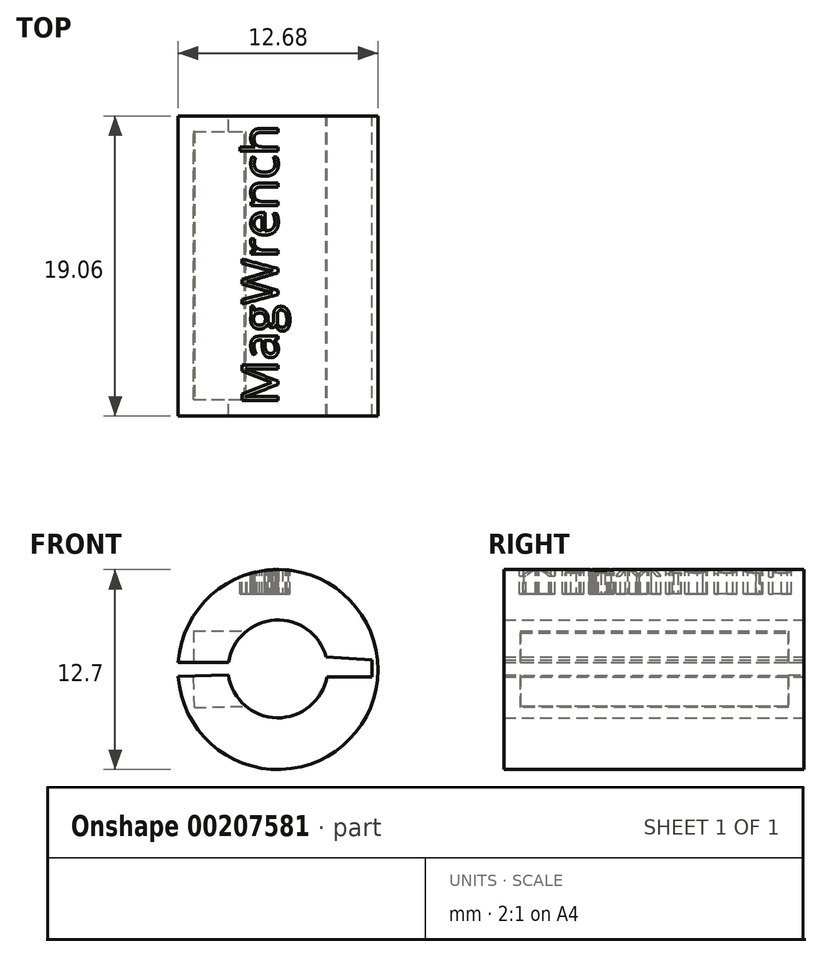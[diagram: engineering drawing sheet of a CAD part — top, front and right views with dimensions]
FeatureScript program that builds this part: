
annotation { "Feature Type Name" : "Feature", "Feature Type Description" : "" }
export const myFeature = defineFeature(function(context is Context, id is Id, definition is map)
    precondition{}
    {
        {
            var Q0;
            Q0=qCreatedBy(makeId("Front.planeOp"),FACE);
            var sketch = newSketch(context, id + "F0", { "sketchPlane" : qUnion([Q0])});
            skArc(sketch, "E0", {"start": v(3.07, 0.8) * mm, "mid": v(-0.17, 3.14) * mm, "end": v(-3.13, 0.45) * mm});
            skArc(sketch, "E1", {"start": v(6.32, 0.58) * mm, "mid": v(-0.06, 6.35) * mm, "end": v(-6.33, 0.46) * mm});
            skArc(sketch, "E2", {"start": v(6.33, -0.46) * mm, "mid": v(6.35, 0.06) * mm, "end": v(6.32, 0.58) * mm});
            skLineSegment(sketch, "E3", {"start": v(3.07, 0.8) * mm, "end": v(5.98, 0.6) * mm});
            skLineSegment(sketch, "E4", {"start": v(3.11, -0.46) * mm, "end": v(5.98, -0.46) * mm});
            skLineSegment(sketch, "E5", {"start": v(5.98, 0.6) * mm, "end": v(5.98, -0.46) * mm});
            skArc(sketch, "E6", {"start": v(-3.15, -0.36) * mm, "mid": v(-0.06, -3.07) * mm, "end": v(3.11, -0.46) * mm});
            skArc(sketch, "E7", {"start": v(-6.33, -0.44) * mm, "mid": v(-0.01, -6.35) * mm, "end": v(6.33, -0.46) * mm});
            skLineSegment(sketch, "E8", {"start": v(-6.33, 0.46) * mm, "end": v(-3.13, 0.45) * mm});
            skLineSegment(sketch, "E9", {"start": v(-6.33, -0.44) * mm, "end": v(-3.15, -0.36) * mm});
            skPoint(sketch, "E10", {"position": v(0, 6.35) * mm});
            skPoint(sketch, "E10.positionSnap0", {"position": v(-0.06, 6.35) * mm});
            skLineSegment(sketch, "E11", {"start": v(-0.17, 3.14) * mm, "end": v(-0.17, -3.06) * mm, "construction": true});
            skPoint(sketch, "E11.startSnap0", {"position": v(-0.17, 3.14) * mm});
            skSolve(sketch);
        }
        {
            var Q0;
            Q0 = qSketchRegion(id + "F0", true);
            extrude(context, id + "F1", {"entities" : qUnion([Q0]), "endBound" : BoundingType.SYMMETRIC, "depth" : 19.05 * mm});
        }
        {
            var Q0;
            Q0=makeQuery(id+"F1.opExtrude","SWEPT_FACE",FACE,{"disambiguationData":[OSD([sQuery(id+"F0.wireOp",EDGE,"E8")])]});
            cPlane(context, id + "F2", {"entities" : qUnion([Q0]), "cplaneType" : CPlaneType.OFFSET, "offset" : 0 * mm, "width" : 152.4 * mm, "height" : 152.4 * mm});
        }
        {
            var Q0;
            Q0=qCreatedBy(id+"F2.planeOp",FACE);
            var sketch = newSketch(context, id + "F3", { "sketchPlane" : qUnion([Q0])});
            skLineSegment(sketch, "E12.bottom", {"start": v(-5.37, 8.48) * mm, "end": v(-3.14, 8.48) * mm});
            skLineSegment(sketch, "E12.top", {"start": v(-5.37, -8.55) * mm, "end": v(-3.14, -8.55) * mm});
            skLineSegment(sketch, "E12.left", {"start": v(-5.37, 8.48) * mm, "end": v(-5.37, -8.55) * mm});
            skLineSegment(sketch, "E12.right", {"start": v(-3.14, 8.48) * mm, "end": v(-3.14, -8.55) * mm});
            skSolve(sketch);
        }
        {
            var Q0;
            Q0 = qSketchRegion(id + "F3", true);
            extrude(context, id + "F4", {"entities" : qUnion([Q0]), "operationType" : NewBodyOperationType.REMOVE, "oppositeDirection" : true, "depth" : 2 * mm});
        }
        {
            var Q0;
            Q0=makeQuery(id+"F1.opExtrude","SWEPT_FACE",FACE,{"disambiguationData":[OSD([sQuery(id+"F0.wireOp",EDGE,"E9")])]});
            cPlane(context, id + "F5", {"entities" : qUnion([Q0]), "cplaneType" : CPlaneType.OFFSET, "offset" : 0 * mm, "width" : 152.4 * mm, "height" : 152.4 * mm});
        }
        {
            var Q0;
            Q0=qCreatedBy(id+"F5.planeOp",FACE);
            var sketch = newSketch(context, id + "F6", { "sketchPlane" : qUnion([Q0])});
            skLineSegment(sketch, "E13.bottom", {"start": v(-5.36, 8.55) * mm, "end": v(-3.12, 8.55) * mm});
            skLineSegment(sketch, "E13.top", {"start": v(-5.36, -8.49) * mm, "end": v(-3.12, -8.49) * mm});
            skLineSegment(sketch, "E13.left", {"start": v(-5.36, 8.55) * mm, "end": v(-5.36, -8.49) * mm});
            skLineSegment(sketch, "E13.right", {"start": v(-3.12, 8.55) * mm, "end": v(-3.12, -8.49) * mm});
            skSolve(sketch);
        }
        {
            var Q0;
            Q0 = qSketchRegion(id + "F6", true);
            var Q1;
            Q1 = qConstructionFilter(qBodyType(qCreatedBy(id + "F6" ,EDGE), BodyType.WIRE), ConstructionObject.NO);
            extrude(context, id + "F7", {"entities" : qUnion([Q0]), "operationType" : NewBodyOperationType.REMOVE, "surfaceEntities" : qUnion([Q1]), "oppositeDirection" : true, "depth" : 2 * mm});
        }
        {
            var Q0;
            Q0=makeQuery(id+"F7.boolean.opBoolean","COPY",FACE,{"derivedFrom":makeQuery(id+"F7.opExtrude","SWEPT_FACE",FACE,{"disambiguationData":[OSD([sQuery(id+"F6.wireOp",EDGE,"E13.right")])]})});
            extrude(context, id + "F8", {"entities" : qUnion([Q0]), "operationType" : NewBodyOperationType.REMOVE, "oppositeDirection" : true, "depth" : 1 * mm});
        }
        {
            var Q0;
            Q0=makeQuery(id+"F4.boolean.opBoolean","COPY",FACE,{"derivedFrom":makeQuery(id+"F4.opExtrude","SWEPT_FACE",FACE,{"disambiguationData":[OSD([sQuery(id+"F3.wireOp",EDGE,"E12.right")])]})});
            extrude(context, id + "F9", {"entities" : qUnion([Q0]), "operationType" : NewBodyOperationType.REMOVE, "oppositeDirection" : true, "depth" : 1 * mm});
        }
        {
            var Q0;
            Q0=makeQuery(id+"F1.opExtrude","CAP_FACE",FACE,{"disambiguationData":[OSD([sQuery(id+"F0.wireOp",EDGE,"E0"),sQuery(id+"F0.wireOp",EDGE,"E1"),sQuery(id+"F0.wireOp",EDGE,"E2"),sQuery(id+"F0.wireOp",EDGE,"E3"),sQuery(id+"F0.wireOp",EDGE,"E4"),sQuery(id+"F0.wireOp",EDGE,"E5"),sQuery(id+"F0.wireOp",EDGE,"E6"),sQuery(id+"F0.wireOp",EDGE,"E7"),sQuery(id+"F0.wireOp",EDGE,"E8"),sQuery(id+"F0.wireOp",EDGE,"E9")])],"isStart":false});
            var sketch = newSketch(context, id + "F10", { "sketchPlane" : qUnion([Q0])});
            skPoint(sketch, "E14", {"position": v(0, 6.35) * mm});
            skSolve(sketch);
        }
        {
            var Q0;
            Q0=sQuery(id+"F10.wireOp",VERTEX,"E14");
            var Q1;
            Q1=qCreatedBy(makeId("Top.planeOp"),FACE);
            cPlane(context, id + "F11", {"entities" : qUnion([Q0, Q1]), "cplaneType" : CPlaneType.PLANE_POINT, "offset" : 25.4 * mm, "width" : 152.4 * mm, "height" : 152.4 * mm});
        }
        {
            var Q0;
            Q0=qCreatedBy(id+"F11.planeOp",FACE);
            var sketch = newSketch(context, id + "F12", { "sketchPlane" : qUnion([Q0])});
            skText(sketch, "E15", { "text": "MagWrench", "fontName": "OpenSans-Regular.ttf"});
            const initialGuessF12  = {"E15": [0, -0.00884, 0, 1, 0.00229]};
            skSetInitialGuess(sketch, initialGuessF12);
            skSolve(sketch);
        }
        {
            var Q0;
            Q0 = qSketchRegion(id + "F12", true);
            extrude(context, id + "F13", {"entities" : qUnion([Q0]), "operationType" : NewBodyOperationType.REMOVE, "oppositeDirection" : true, "depth" : 1.55 * mm});
        }
    });
